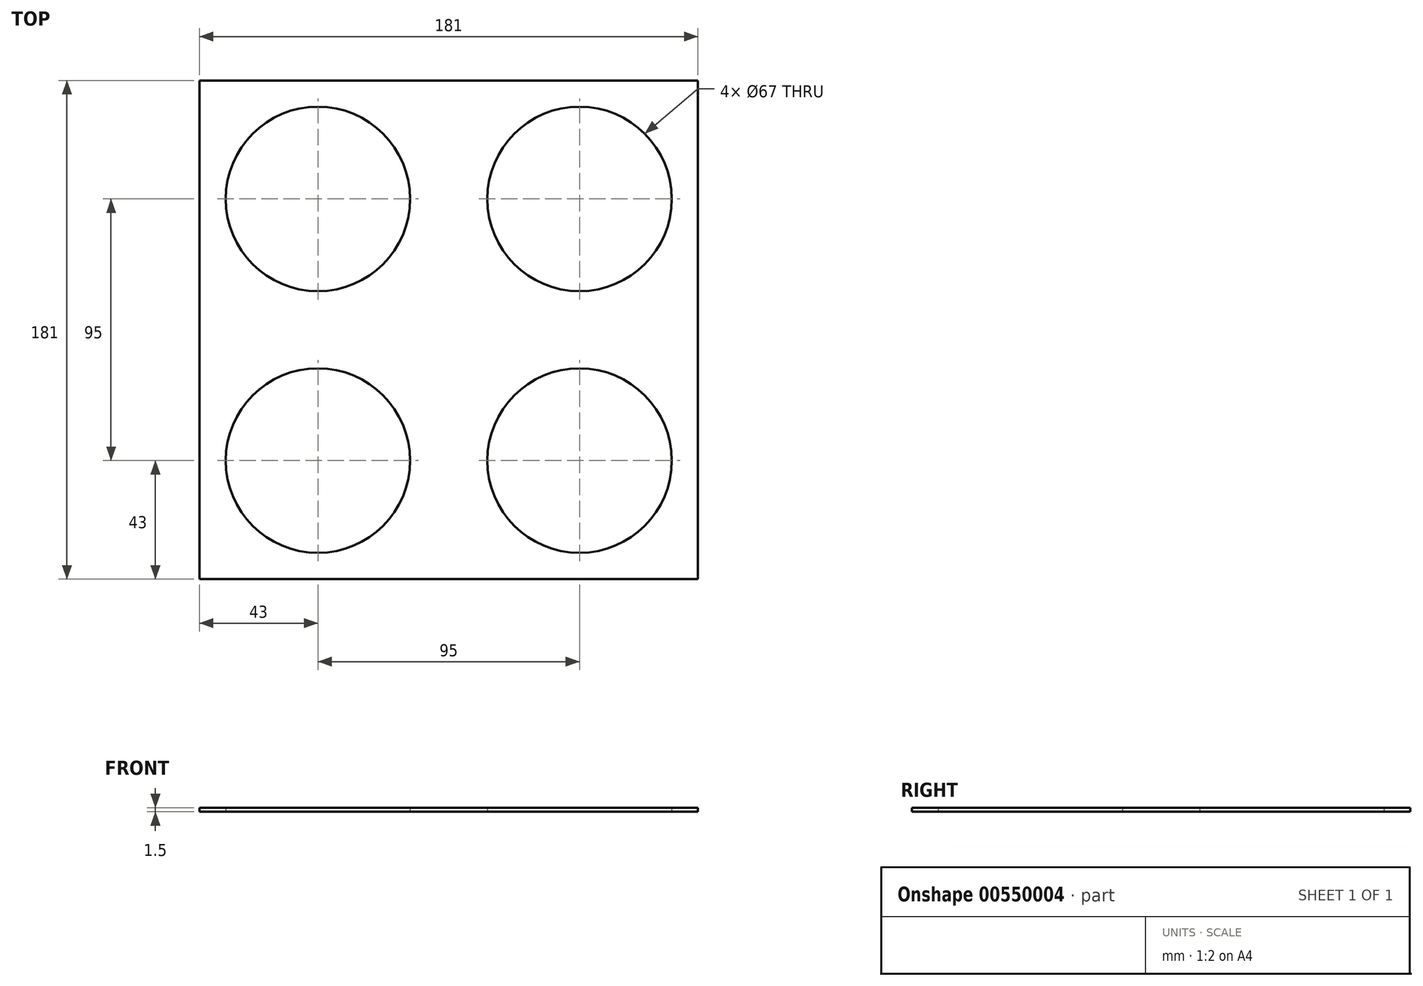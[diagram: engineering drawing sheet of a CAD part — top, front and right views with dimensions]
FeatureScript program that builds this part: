
annotation { "Feature Type Name" : "Feature", "Feature Type Description" : "" }
export const myFeature = defineFeature(function(context is Context, id is Id, definition is map)
    precondition{}
    {
        {
            var Q0;
            Q0=qCreatedBy(makeId("Top.planeOp"),FACE);
            var sketch = newSketch(context, id + "F0", { "sketchPlane" : qUnion([Q0])});
            skPoint(sketch, "E0.middle", {"position": v(0, 0) * mm});
            skCircle(sketch, "E1", {"center": v(-47.5, 47.5) * mm, "radius": 33.5 * mm});
            skCircle(sketch, "E2", {"center": v(47.5, 47.5) * mm, "radius": 33.5 * mm});
            skCircle(sketch, "E3", {"center": v(47.5, -47.5) * mm, "radius": 33.5 * mm});
            skCircle(sketch, "E4", {"center": v(-47.5, -47.5) * mm, "radius": 33.5 * mm});
            skLineSegment(sketch, "E5.bottom", {"start": v(90.5, 90.5) * mm, "end": v(-90.5, 90.5) * mm});
            skLineSegment(sketch, "E5.top", {"start": v(90.5, -90.5) * mm, "end": v(-90.5, -90.5) * mm});
            skLineSegment(sketch, "E5.left", {"start": v(90.5, 90.5) * mm, "end": v(90.5, -90.5) * mm});
            skLineSegment(sketch, "E5.right", {"start": v(-90.5, 90.5) * mm, "end": v(-90.5, -90.5) * mm});
            skSolve(sketch);
        }
        {
            var Q0;
            Q0 = qSketchRegion(id + "F0", true);
            extrude(context, id + "F1", {"entities" : qUnion([Q0]), "depth" : 1.5 * mm, "offsetDistance" : 25 * mm});
        }
    });
